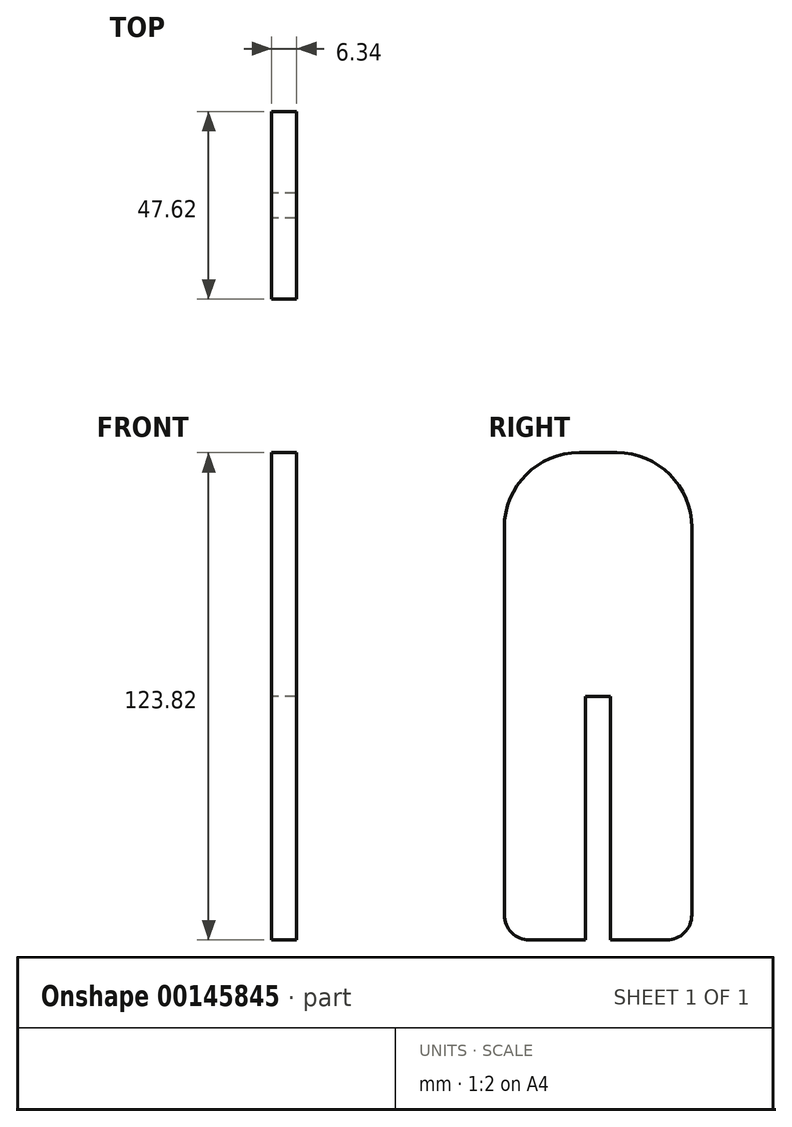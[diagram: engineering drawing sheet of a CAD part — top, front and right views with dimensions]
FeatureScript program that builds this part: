
annotation { "Feature Type Name" : "Feature", "Feature Type Description" : "" }
export const myFeature = defineFeature(function(context is Context, id is Id, definition is map)
    precondition{}
    {
        {
            var Q0;
            Q0=qCreatedBy(makeId("Right.planeOp"),FACE);
            var sketch = newSketch(context, id + "F0", { "sketchPlane" : qUnion([Q0])});
            skLineSegment(sketch, "E0.bottom", {"start": v(-4.76, 61.91) * mm, "end": v(4.76, 61.91) * mm});
            skLineSegment(sketch, "E0.top", {"start": v(-17.46, -61.91) * mm, "end": v(-3.17, -61.91) * mm});
            skLineSegment(sketch, "E0.left", {"start": v(-23.81, 42.86) * mm, "end": v(-23.81, -55.56) * mm});
            skLineSegment(sketch, "E0.right", {"start": v(23.81, 42.86) * mm, "end": v(23.81, -55.56) * mm});
            skPoint(sketch, "E0.middle", {"position": v(0, 0) * mm});
            skPoint(sketch, "E1.visualSharp", {"position": v(-23.81, 61.91) * mm});
            skArc(sketch, "E1.filletArc", {"start": v(-4.76, 61.91) * mm, "mid": v(-18.23, 56.33) * mm, "end": v(-23.81, 42.86) * mm});
            skPoint(sketch, "E2.visualSharp", {"position": v(23.81, 61.91) * mm});
            skArc(sketch, "E2.filletArc", {"start": v(23.81, 42.86) * mm, "mid": v(18.23, 56.33) * mm, "end": v(4.76, 61.91) * mm});
            skLineSegment(sketch, "E3", {"start": v(3.18, -61.91) * mm, "end": v(3.18, 0) * mm});
            skLineSegment(sketch, "E4", {"start": v(3.18, 0) * mm, "end": v(-3.17, 0) * mm});
            skLineSegment(sketch, "E5", {"start": v(-3.17, 0) * mm, "end": v(-3.17, -61.91) * mm});
            skLineSegment(sketch, "E6.trimOffspring", {"start": v(3.18, -61.91) * mm, "end": v(17.46, -61.91) * mm});
            skPoint(sketch, "E7.visualSharp", {"position": v(-23.81, -61.91) * mm});
            skArc(sketch, "E7.filletArc", {"start": v(-23.81, -55.56) * mm, "mid": v(-21.95, -60.05) * mm, "end": v(-17.46, -61.91) * mm});
            skPoint(sketch, "E8.visualSharp", {"position": v(23.81, -61.91) * mm});
            skArc(sketch, "E8.filletArc", {"start": v(17.46, -61.91) * mm, "mid": v(21.95, -60.05) * mm, "end": v(23.81, -55.56) * mm});
            skSolve(sketch);
        }
        {
            var Q0;
            Q0=qSketchRegion(id+"F0",true);
            extrude(context, id + "F1", {"entities" : qUnion([Q0]), "endBound" : BoundingType.SYMMETRIC, "depth" : 6.35 * mm});
        }
    });
